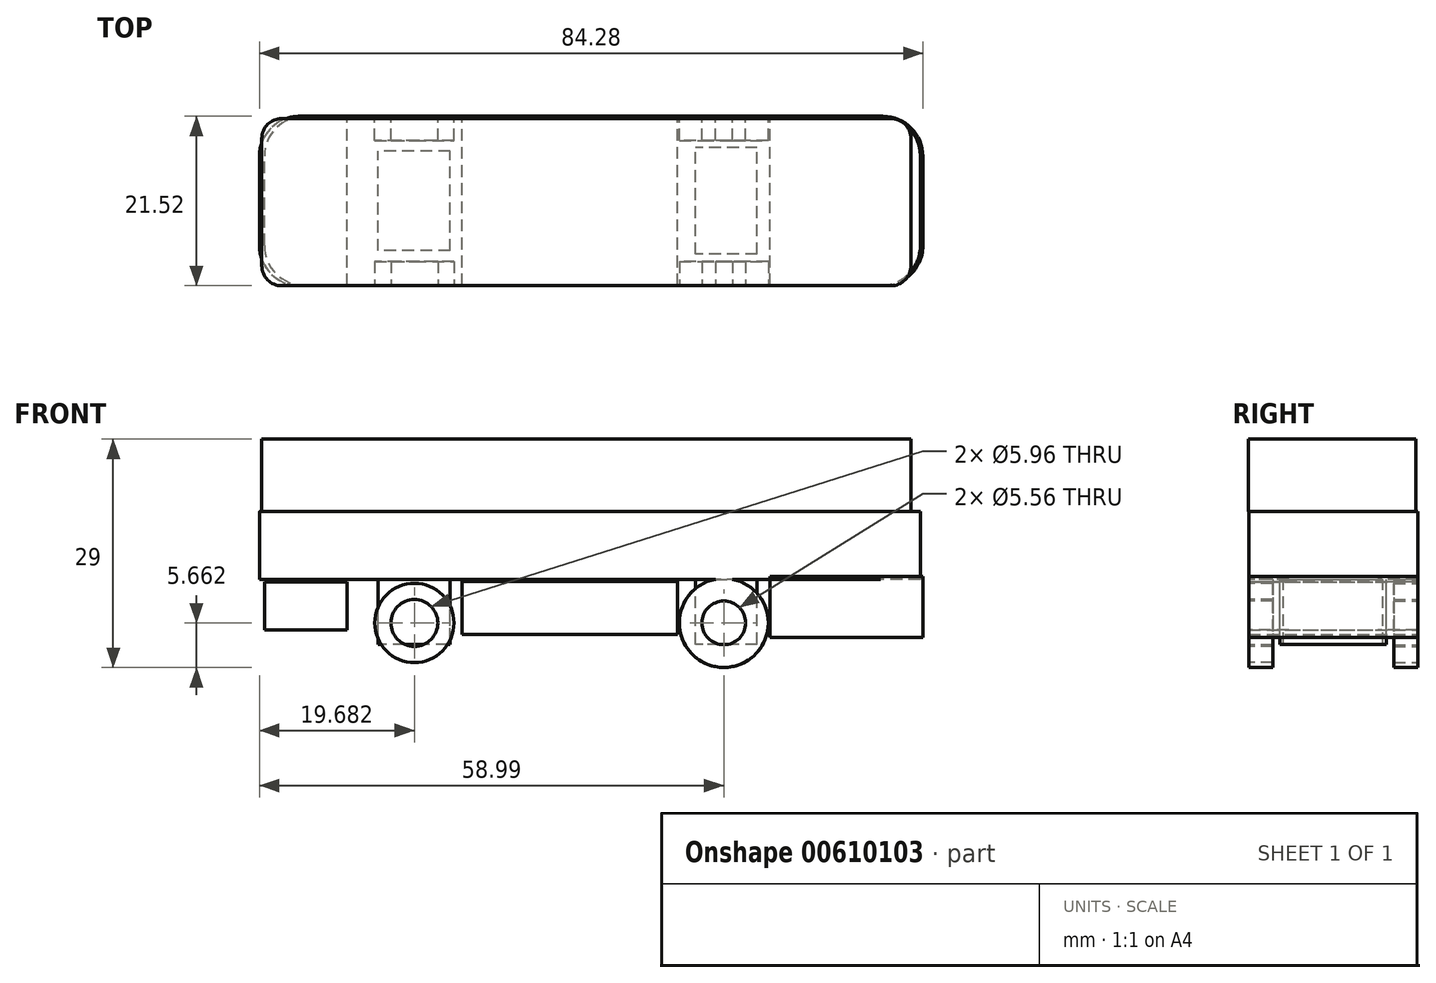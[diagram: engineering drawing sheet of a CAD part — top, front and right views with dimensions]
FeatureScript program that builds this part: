
annotation { "Feature Type Name" : "Feature", "Feature Type Description" : "" }
export const myFeature = defineFeature(function(context is Context, id is Id, definition is map)
    precondition{}
    {
        {
            var Q0;
            Q0=qCreatedBy(makeId("Front.planeOp"),FACE);
            var sketch = newSketch(context, id + "F0", { "sketchPlane" : qUnion([Q0])});
            skLineSegment(sketch, "E0.bottom", {"start": v(-33.62, 0) * mm, "end": v(50.34, 0) * mm});
            skLineSegment(sketch, "E0.top", {"start": v(-33.62, -8.6) * mm, "end": v(50.34, -8.6) * mm});
            skLineSegment(sketch, "E0.left", {"start": v(-33.62, 0) * mm, "end": v(-33.62, -8.6) * mm});
            skLineSegment(sketch, "E0.right", {"start": v(50.34, 0) * mm, "end": v(50.34, -8.6) * mm});
            skSolve(sketch);
        }
        {
            var Q0;
            Q0=qCreatedBy(makeId("Front.planeOp"),FACE);
            var sketch = newSketch(context, id + "F1", { "sketchPlane" : qUnion([Q0])});
            skLineSegment(sketch, "E1.bottom", {"start": v(-32.98, -8.94) * mm, "end": v(-22.5, -8.94) * mm});
            skLineSegment(sketch, "E1.top", {"start": v(-32.98, -15.02) * mm, "end": v(-22.5, -15.02) * mm});
            skLineSegment(sketch, "E1.left", {"start": v(-32.98, -8.94) * mm, "end": v(-32.98, -15.02) * mm});
            skLineSegment(sketch, "E1.right", {"start": v(-22.5, -8.94) * mm, "end": v(-22.5, -15.02) * mm});
            skLineSegment(sketch, "E2.bottom", {"start": v(-7.86, -8.9) * mm, "end": v(19.5, -8.9) * mm});
            skLineSegment(sketch, "E2.top", {"start": v(-7.86, -15.64) * mm, "end": v(19.5, -15.64) * mm});
            skLineSegment(sketch, "E2.left", {"start": v(-7.86, -8.9) * mm, "end": v(-7.86, -15.64) * mm});
            skLineSegment(sketch, "E2.right", {"start": v(19.5, -8.9) * mm, "end": v(19.5, -15.64) * mm});
            skLineSegment(sketch, "E3.bottom", {"start": v(31.26, -8.26) * mm, "end": v(50.66, -8.26) * mm});
            skLineSegment(sketch, "E3.top", {"start": v(31.26, -16) * mm, "end": v(50.66, -16) * mm});
            skLineSegment(sketch, "E3.left", {"start": v(31.26, -8.26) * mm, "end": v(31.26, -16) * mm});
            skLineSegment(sketch, "E3.right", {"start": v(50.66, -8.26) * mm, "end": v(50.66, -16) * mm});
            skSolve(sketch);
        }
        {
            var Q0;
            Q0 = qSketchRegion(id + "FR8kGcHlPAdUBtf_0", true);
            var Q1;
            Q1=makeQuery(id+"F0.imprint","IMPRINT",FACE,{"disambiguationData":[TD([[makeQuery(id+"F0.imprint","IMPRINT",EDGE,{"derivedFrom":sQuery(id+"F0.wireOp",EDGE,"E0.bottom")}),-1.0]])]});
            var Q2;
            Q2=makeQuery(id+"F1.imprint","IMPRINT",FACE,{"disambiguationData":[TD([[makeQuery(id+"F1.imprint","IMPRINT",EDGE,{"derivedFrom":sQuery(id+"F1.wireOp",EDGE,"E2.bottom")}),-1.0]])]});
            var Q3;
            Q3=makeQuery(id+"F1.imprint","IMPRINT",FACE,{"disambiguationData":[TD([[makeQuery(id+"F1.imprint","IMPRINT",EDGE,{"derivedFrom":sQuery(id+"F1.wireOp",EDGE,"E3.bottom")}),-1.0]])]});
            var Q4;
            Q4=makeQuery(id+"F1.imprint","IMPRINT",FACE,{"disambiguationData":[TD([[makeQuery(id+"F1.imprint","IMPRINT",EDGE,{"derivedFrom":sQuery(id+"F1.wireOp",EDGE,"E1.bottom")}),-1.0]])]});
            extrude(context, id + "F2", {"entities" : qUnion([Q0, Q1, Q2, Q3, Q4]), "endBound" : BoundingType.SYMMETRIC, "depth" : 21.5 * mm, "offsetDistance" : 25.4 * mm});
        }
        {
            var Q0;
            Q0=makeQuery(id+"F2.opExtrude","CAP_FACE",FACE,{"disambiguationData":[OSD([sQuery(id+"F0.wireOp",EDGE,"E0.bottom"),sQuery(id+"F0.wireOp",EDGE,"E0.top"),sQuery(id+"F0.wireOp",EDGE,"E0.left"),sQuery(id+"F0.wireOp",EDGE,"E0.right")])],"isStart":true});
            var sketch = newSketch(context, id + "F3", { "sketchPlane" : qUnion([Q0])});
            skCircle(sketch, "E4", {"center": v(-25.37, -14.16) * mm, "radius": 5.66 * mm});
            skCircle(sketch, "E5", {"center": v(13.94, -14.16) * mm, "radius": 5.03 * mm});
            skCircle(sketch, "E6", {"center": v(13.94, -14.16) * mm, "radius": 2.98 * mm});
            skCircle(sketch, "E7", {"center": v(-25.37, -14.16) * mm, "radius": 2.78 * mm});
            skSolve(sketch);
        }
        {
            var Q0;
            Q0=makeQuery(id+"F2.opExtrude","CAP_EDGE",EDGE,{"disambiguationData":[OSD([sQuery(id+"F0.wireOp",EDGE,"E0.right")])],"isStart":true});
            var Q1;
            Q1=makeQuery(id+"F2.opExtrude","CAP_EDGE",EDGE,{"disambiguationData":[OSD([sQuery(id+"F0.wireOp",EDGE,"E0.right")])],"isStart":false});
            fillet(context, id + "F4", {"entities" : qUnion([Q0, Q1]), "radius" : 5.08 * mm, "tangentPropagation" : true, "allowEdgeOverflow" : false});
        }
        {
            var Q0;
            Q0=makeQuery(id+"F2.opExtrude","CAP_EDGE",EDGE,{"disambiguationData":[OSD([sQuery(id+"F1.wireOp",EDGE,"E3.right")])],"isStart":true});
            var Q1;
            Q1=makeQuery(id+"F2.opExtrude","CAP_EDGE",EDGE,{"disambiguationData":[OSD([sQuery(id+"F1.wireOp",EDGE,"E3.right")])],"isStart":false});
            fillet(context, id + "F5", {"entities" : qUnion([Q0, Q1]), "radius" : 5.08 * mm, "tangentPropagation" : true, "allowEdgeOverflow" : false});
        }
        {
            var Q0;
            Q0 = qSketchRegion(id + "F3", true);
            extrude(context, id + "F6", {"entities" : qUnion([Q0]), "oppositeDirection" : true, "depth" : 3.07 * mm, "offsetDistance" : 25.4 * mm});
        }
        {
            var Q0;
            Q0=makeQuery(id+"F2.opExtrude","CAP_EDGE",EDGE,{"disambiguationData":[OSD([sQuery(id+"F0.wireOp",EDGE,"E0.left")])],"isStart":false});
            var Q1;
            Q1=makeQuery(id+"F2.opExtrude","CAP_EDGE",EDGE,{"disambiguationData":[OSD([sQuery(id+"F0.wireOp",EDGE,"E0.left")])],"isStart":true});
            fillet(context, id + "F7", {"entities" : qUnion([Q0, Q1]), "radius" : 5.08 * mm, "tangentPropagation" : true, "allowEdgeOverflow" : false});
        }
        {
            var Q0;
            Q0=makeQuery(id+"F2.opExtrude","CAP_EDGE",EDGE,{"disambiguationData":[OSD([sQuery(id+"F1.wireOp",EDGE,"E1.left")])],"isStart":true});
            var Q1;
            Q1=makeQuery(id+"F2.opExtrude","CAP_EDGE",EDGE,{"disambiguationData":[OSD([sQuery(id+"F1.wireOp",EDGE,"E1.left")])],"isStart":false});
            fillet(context, id + "F8", {"entities" : qUnion([Q0, Q1]), "radius" : 5.08 * mm, "tangentPropagation" : true, "allowEdgeOverflow" : false});
        }
        {
            var Q0;
            Q0=makeQuery(id+"F6.opExtrude","SWEPT_BODY",BODY,{"disambiguationData":[OSD([sQuery(id+"F3.wireOp",EDGE,"E4"),sQuery(id+"F3.wireOp",EDGE,"E7")])]});
            var Q1;
            Q1=makeQuery(id+"F6.opExtrude","SWEPT_BODY",BODY,{"disambiguationData":[OSD([sQuery(id+"F3.wireOp",EDGE,"E5"),sQuery(id+"F3.wireOp",EDGE,"E6")])]});
            var Q2;
            Q2=qCreatedBy(makeId("Front.planeOp"),FACE);
            mirror(context, id + "F9", {"operationType" : NewBodyOperationType.ADD, "entities" : qUnion([Q0, Q1]), "mirrorPlane" : qUnion([Q2])});
        }
        {
            var Q0;
            Q0=qCreatedBy(makeId("Top.planeOp"),FACE);
            var sketch = newSketch(context, id + "F10", { "sketchPlane" : qUnion([Q0])});
            skLineSegment(sketch, "E8.bottom", {"start": v(-9.37, -6.31) * mm, "end": v(-18.57, -6.31) * mm});
            skLineSegment(sketch, "E8.top", {"start": v(-9.37, 6.31) * mm, "end": v(-18.57, 6.31) * mm});
            skLineSegment(sketch, "E8.left", {"start": v(-9.37, -6.31) * mm, "end": v(-9.37, 6.31) * mm});
            skLineSegment(sketch, "E8.right", {"start": v(-18.57, -6.31) * mm, "end": v(-18.57, 6.31) * mm});
            skPoint(sketch, "E8.middle", {"position": v(-13.97, 0) * mm});
            skLineSegment(sketch, "E9.bottom", {"start": v(29.6, -6.77) * mm, "end": v(21.74, -6.77) * mm});
            skLineSegment(sketch, "E9.top", {"start": v(29.6, 6.77) * mm, "end": v(21.74, 6.77) * mm});
            skLineSegment(sketch, "E9.left", {"start": v(29.6, -6.77) * mm, "end": v(29.6, 6.77) * mm});
            skLineSegment(sketch, "E9.right", {"start": v(21.74, -6.77) * mm, "end": v(21.74, 6.77) * mm});
            skPoint(sketch, "E9.middle", {"position": v(25.67, 0) * mm});
            skSolve(sketch);
        }
        {
            var Q0;
            Q0=makeQuery(id+"F10.imprint","IMPRINT",FACE,{"disambiguationData":[TD([[makeQuery(id+"F10.imprint","IMPRINT",EDGE,{"derivedFrom":sQuery(id+"F10.wireOp",EDGE,"E8.bottom")}),-1.0]])]});
            var Q1;
            Q1=makeQuery(id+"F10.imprint","IMPRINT",FACE,{"disambiguationData":[TD([[makeQuery(id+"F10.imprint","IMPRINT",EDGE,{"derivedFrom":sQuery(id+"F10.wireOp",EDGE,"E9.bottom")}),-1.0]])]});
            extrude(context, id + "F11", {"entities" : qUnion([Q0, Q1]), "operationType" : NewBodyOperationType.ADD, "oppositeDirection" : true, "depth" : 16.87 * mm, "offsetDistance" : 25.4 * mm});
        }
        {
            var Q0;
            Q0=qCreatedBy(makeId("Front.planeOp"),FACE);
            var sketch = newSketch(context, id + "F12", { "sketchPlane" : qUnion([Q0])});
            skCircle(sketch, "E10", {"center": v(25.84, -14.2) * mm, "radius": 1.03 * mm});
            skCircle(sketch, "E11", {"center": v(-13.54, -14.2) * mm, "radius": 0.79 * mm});
            skSolve(sketch);
        }
        {
            var Q0;
            Q0=sQuery(id+"F12.wireOp",EDGE,"E10");
            extrude(context, id + "F13", {"bodyType" : ToolBodyType.SURFACE, "surfaceEntities" : qUnion([Q0]), "depth" : 10.54 * mm, "offsetDistance" : 25.4 * mm});
        }
        {
            var Q0;
            Q0=qCreatedBy(makeId("Front.planeOp"),FACE);
            var sketch = newSketch(context, id + "F14", { "sketchPlane" : qUnion([Q0])});
            skCircle(sketch, "E12", {"center": v(-13.86, -13.83) * mm, "radius": 1.23 * mm});
            skSolve(sketch);
        }
        {
            var Q0;
            Q0=sQuery(id+"F14.wireOp",EDGE,"E12");
            extrude(context, id + "F15", {"bodyType" : ToolBodyType.SURFACE, "surfaceEntities" : qUnion([Q0]), "depth" : 10.62 * mm, "offsetDistance" : 25.4 * mm});
        }
        {
            var Q0;
            Q0=qCreatedBy(makeId("Front.planeOp"),FACE);
            var sketch = newSketch(context, id + "F16", { "sketchPlane" : qUnion([Q0])});
            skCircle(sketch, "E13", {"center": v(25.65, -14.11) * mm, "radius": 0.9 * mm});
            skCircle(sketch, "E14", {"center": v(-13.65, -14.17) * mm, "radius": 0.82 * mm});
            skSolve(sketch);
        }
        {
            var Q0;
            Q0=sQuery(id+"F16.wireOp",EDGE,"E13");
            extrude(context, id + "F17", {"bodyType" : ToolBodyType.SURFACE, "surfaceEntities" : qUnion([Q0]), "oppositeDirection" : true, "depth" : 10.5 * mm, "offsetDistance" : 25.4 * mm});
        }
        {
            var Q0;
            Q0=qCreatedBy(makeId("Front.planeOp"),FACE);
            var sketch = newSketch(context, id + "F18", { "sketchPlane" : qUnion([Q0])});
            skCircle(sketch, "E15", {"center": v(-13.78, -14.14) * mm, "radius": 0.96 * mm});
            skSolve(sketch);
        }
        {
            var Q0;
            Q0=sQuery(id+"F18.wireOp",EDGE,"E15");
            extrude(context, id + "F19", {"bodyType" : ToolBodyType.SURFACE, "surfaceEntities" : qUnion([Q0]), "oppositeDirection" : true, "depth" : 10.77 * mm, "offsetDistance" : 25.4 * mm});
        }
        {
            var Q0;
            Q0=qCreatedBy(makeId("Right.planeOp"),FACE);
            var sketch = newSketch(context, id + "F20", { "sketchPlane" : qUnion([Q0])});
            skLineSegment(sketch, "E16.bottom", {"start": v(-10.77, 0) * mm, "end": v(10.47, 0) * mm});
            skLineSegment(sketch, "E16.top", {"start": v(-10.77, 9.18) * mm, "end": v(10.47, 9.18) * mm});
            skLineSegment(sketch, "E16.left", {"start": v(-10.77, 0) * mm, "end": v(-10.77, 9.18) * mm});
            skLineSegment(sketch, "E16.right", {"start": v(10.47, 0) * mm, "end": v(10.47, 9.18) * mm});
            skSolve(sketch);
        }
        {
            var Q0;
            Q0=makeQuery(id+"F20.imprint","IMPRINT",FACE,{"disambiguationData":[TD([[makeQuery(id+"F20.imprint","IMPRINT",EDGE,{"derivedFrom":sQuery(id+"F20.wireOp",EDGE,"E16.bottom")}),1.0]])]});
            extrude(context, id + "F21", {"entities" : qUnion([Q0]), "operationType" : NewBodyOperationType.ADD, "depth" : 49.14 * mm, "offsetDistance" : 25.4 * mm});
        }
        {
            var Q0;
            Q0=makeQuery(id+"F21.opExtrude","CAP_EDGE",EDGE,{"disambiguationData":[OSD([sQuery(id+"F20.wireOp",EDGE,"E16.left")])],"isStart":false});
            var Q1;
            Q1=makeQuery(id+"F21.opExtrude","CAP_EDGE",EDGE,{"disambiguationData":[OSD([sQuery(id+"F20.wireOp",EDGE,"E16.right")])],"isStart":false});
            fillet(context, id + "F22", {"entities" : qUnion([Q0, Q1]), "radius" : 2.54 * mm, "tangentPropagation" : true, "allowEdgeOverflow" : false});
        }
        {
            var Q0;
            Q0=makeQuery(id+"F21.opExtrude","CAP_FACE",FACE,{"disambiguationData":[OSD([sQuery(id+"F20.wireOp",EDGE,"E16.bottom"),sQuery(id+"F20.wireOp",EDGE,"E16.top"),sQuery(id+"F20.wireOp",EDGE,"E16.left"),sQuery(id+"F20.wireOp",EDGE,"E16.right")])],"isStart":true});
            extrude(context, id + "F23", {"entities" : qUnion([Q0]), "operationType" : NewBodyOperationType.ADD, "depth" : 33.32 * mm, "offsetDistance" : 25.4 * mm});
        }
        {
            var Q0;
            Q0=makeQuery(id+"F23.opExtrude","CAP_EDGE",EDGE,{"disambiguationData":[OSD([sQuery(id+"F20.wireOp",EDGE,"E16.right")])],"isStart":false});
            var Q1;
            Q1=makeQuery(id+"F23.opExtrude","CAP_EDGE",EDGE,{"disambiguationData":[OSD([sQuery(id+"F20.wireOp",EDGE,"E16.left")])],"isStart":false});
            fillet(context, id + "F24", {"entities" : qUnion([Q0, Q1]), "radius" : 2.54 * mm, "tangentPropagation" : true, "allowEdgeOverflow" : false});
        }
    });
